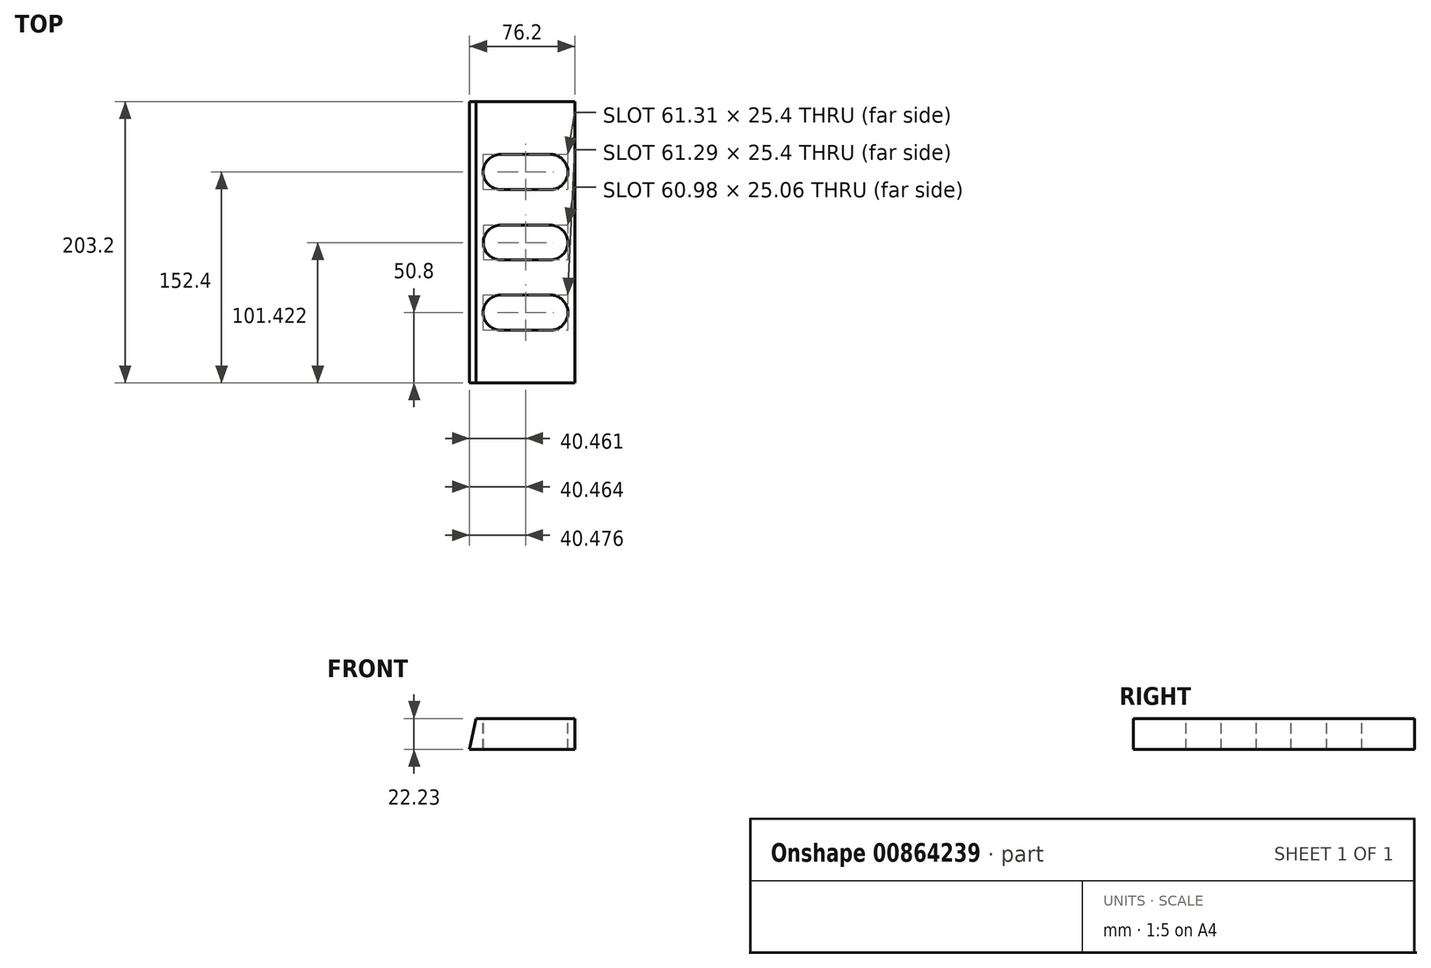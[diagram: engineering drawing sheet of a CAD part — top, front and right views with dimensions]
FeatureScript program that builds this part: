
annotation { "Feature Type Name" : "Feature", "Feature Type Description" : "" }
export const myFeature = defineFeature(function(context is Context, id is Id, definition is map)
    precondition{}
    {
        {
            var Q0;
            Q0=qCreatedBy(makeId("Front.planeOp"),FACE);
            var sketch = newSketch(context, id + "F0", { "sketchPlane" : qUnion([Q0])});
            skLineSegment(sketch, "E0", {"start": v(0, 0) * mm, "end": v(76.2, 0) * mm});
            skLineSegment(sketch, "E1", {"start": v(76.2, 0) * mm, "end": v(76.2, 22.22) * mm});
            skLineSegment(sketch, "E2", {"start": v(4.72, 22.22) * mm, "end": v(76.2, 22.22) * mm});
            skLineSegment(sketch, "E3", {"start": v(4.72, 22.22) * mm, "end": v(0, 0) * mm});
            skSolve(sketch);
        }
        {
            var Q0;
            Q0 = qSketchRegion(id + "F0", true);
            extrude(context, id + "F1", {"entities" : qUnion([Q0]), "depth" : 203.2 * mm, "offsetDistance" : 25.4 * mm});
        }
        {
            var Q0;
            Q0 = qSketchRegion(id + "F0", true);
            extrude(context, id + "F2", {"entities" : qUnion([Q0]), "operationType" : NewBodyOperationType.ADD, "depth" : 203.2 * mm, "offsetDistance" : 25.4 * mm});
        }
        {
            var Q0;
            Q0=makeQuery(id+"F1.opExtrude","SWEPT_FACE",FACE,{"disambiguationData":[OSD([sQuery(id+"F0.wireOp",EDGE,"E2")])]});
            var sketch = newSketch(context, id + "F3", { "sketchPlane" : qUnion([Q0])});
            skArc(sketch, "E4", {"start": v(22.5, -38.1) * mm, "mid": v(9.8, -50.8) * mm, "end": v(22.5, -63.49) * mm});
            skArc(sketch, "E5", {"start": v(58.42, -63.5) * mm, "mid": v(71.12, -50.8) * mm, "end": v(58.42, -38.1) * mm});
            skArc(sketch, "E6", {"start": v(22.5, -89.25) * mm, "mid": v(9.97, -101.78) * mm, "end": v(22.5, -114.3) * mm});
            skArc(sketch, "E7", {"start": v(58.42, -114.3) * mm, "mid": v(70.95, -101.78) * mm, "end": v(58.42, -89.25) * mm});
            skArc(sketch, "E8", {"start": v(22.5, -139.73) * mm, "mid": v(9.83, -152.4) * mm, "end": v(22.5, -165.07) * mm});
            skArc(sketch, "E9", {"start": v(58.4, -165.1) * mm, "mid": v(71.12, -152.4) * mm, "end": v(58.41, -139.7) * mm});
            skArc(sketch, "E10.MirrorC", {"start": v(22.5, -63.49) * mm, "mid": v(9.81, -50.8) * mm, "end": v(22.5, -38.1) * mm});
            skArc(sketch, "E11.MirrorC", {"start": v(58.42, -38.1) * mm, "mid": v(71.12, -50.8) * mm, "end": v(58.42, -63.5) * mm});
            skLineSegment(sketch, "E12", {"start": v(22.5, -38.1) * mm, "end": v(58.42, -38.1) * mm});
            skLineSegment(sketch, "E13", {"start": v(22.5, -63.49) * mm, "end": v(58.42, -63.5) * mm});
            skLineSegment(sketch, "E14", {"start": v(22.5, -89.25) * mm, "end": v(58.42, -89.25) * mm});
            skLineSegment(sketch, "E15", {"start": v(22.22, -114.3) * mm, "end": v(58.42, -114.3) * mm});
            skLineSegment(sketch, "E16", {"start": v(22.5, -139.73) * mm, "end": v(58.42, -139.7) * mm});
            skLineSegment(sketch, "E17", {"start": v(22.5, -165.07) * mm, "end": v(58.42, -165.1) * mm});
            skSolve(sketch);
        }
        {
            var Q0;
            Q0 = qSketchRegion(id + "F3", true);
            extrude(context, id + "F4", {"entities" : qUnion([Q0]), "operationType" : NewBodyOperationType.REMOVE, "oppositeDirection" : true, "depth" : 25.4 * mm, "offsetDistance" : 25.4 * mm});
        }
    });
